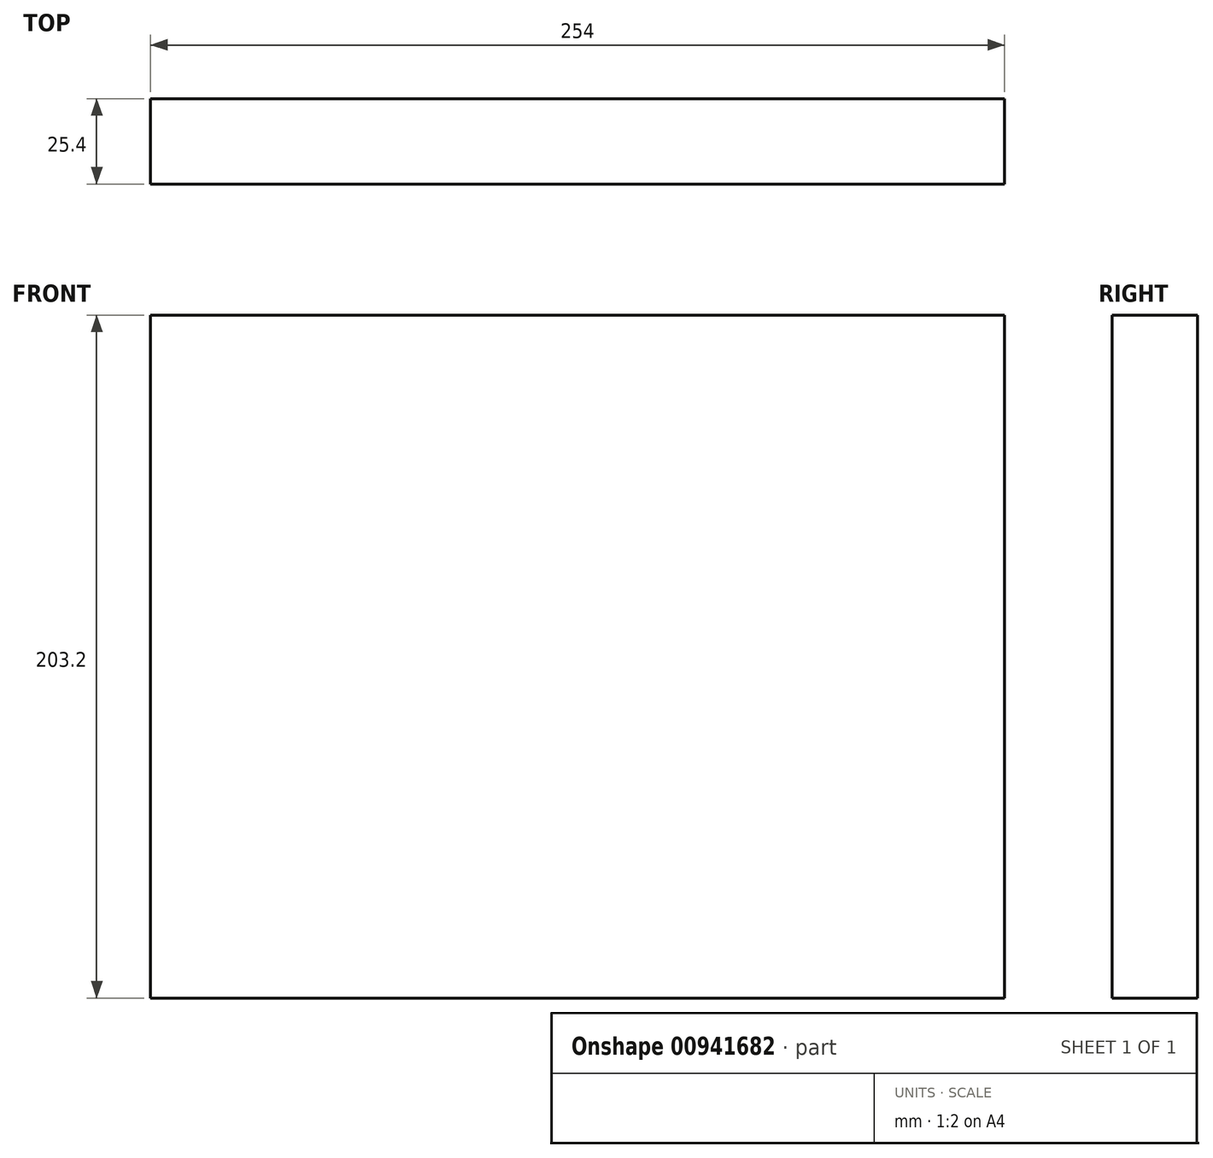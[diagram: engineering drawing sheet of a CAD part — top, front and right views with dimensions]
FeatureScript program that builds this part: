
annotation { "Feature Type Name" : "Feature", "Feature Type Description" : "" }
export const myFeature = defineFeature(function(context is Context, id is Id, definition is map)
    precondition{}
    {
        {
            var Q0;
            Q0=qCreatedBy(makeId("Front.planeOp"),FACE);
            var sketch = newSketch(context, id + "F0", { "sketchPlane" : qUnion([Q0])});
            skLineSegment(sketch, "E0.bottom", {"start": v(-120.47, 109.36) * mm, "end": v(133.53, 109.36) * mm});
            skLineSegment(sketch, "E0.top", {"start": v(-120.47, -93.84) * mm, "end": v(133.53, -93.84) * mm});
            skLineSegment(sketch, "E0.left", {"start": v(-120.47, 109.36) * mm, "end": v(-120.47, -93.84) * mm});
            skLineSegment(sketch, "E0.right", {"start": v(133.53, 109.36) * mm, "end": v(133.53, -93.84) * mm});
            skSolve(sketch);
        }
        {
            var Q0;
            Q0=makeQuery(id+"F0.imprint","IMPRINT",FACE,{"disambiguationData":[TD([[makeQuery(id+"F0.imprint","IMPRINT",EDGE,{"derivedFrom":sQuery(id+"F0.wireOp",EDGE,"E0.bottom")}),-1.0]])]});
            extrude(context, id + "F1", {"entities" : qUnion([Q0]), "depth" : 25.4 * mm, "offsetDistance" : 25.4 * mm});
        }
    });
